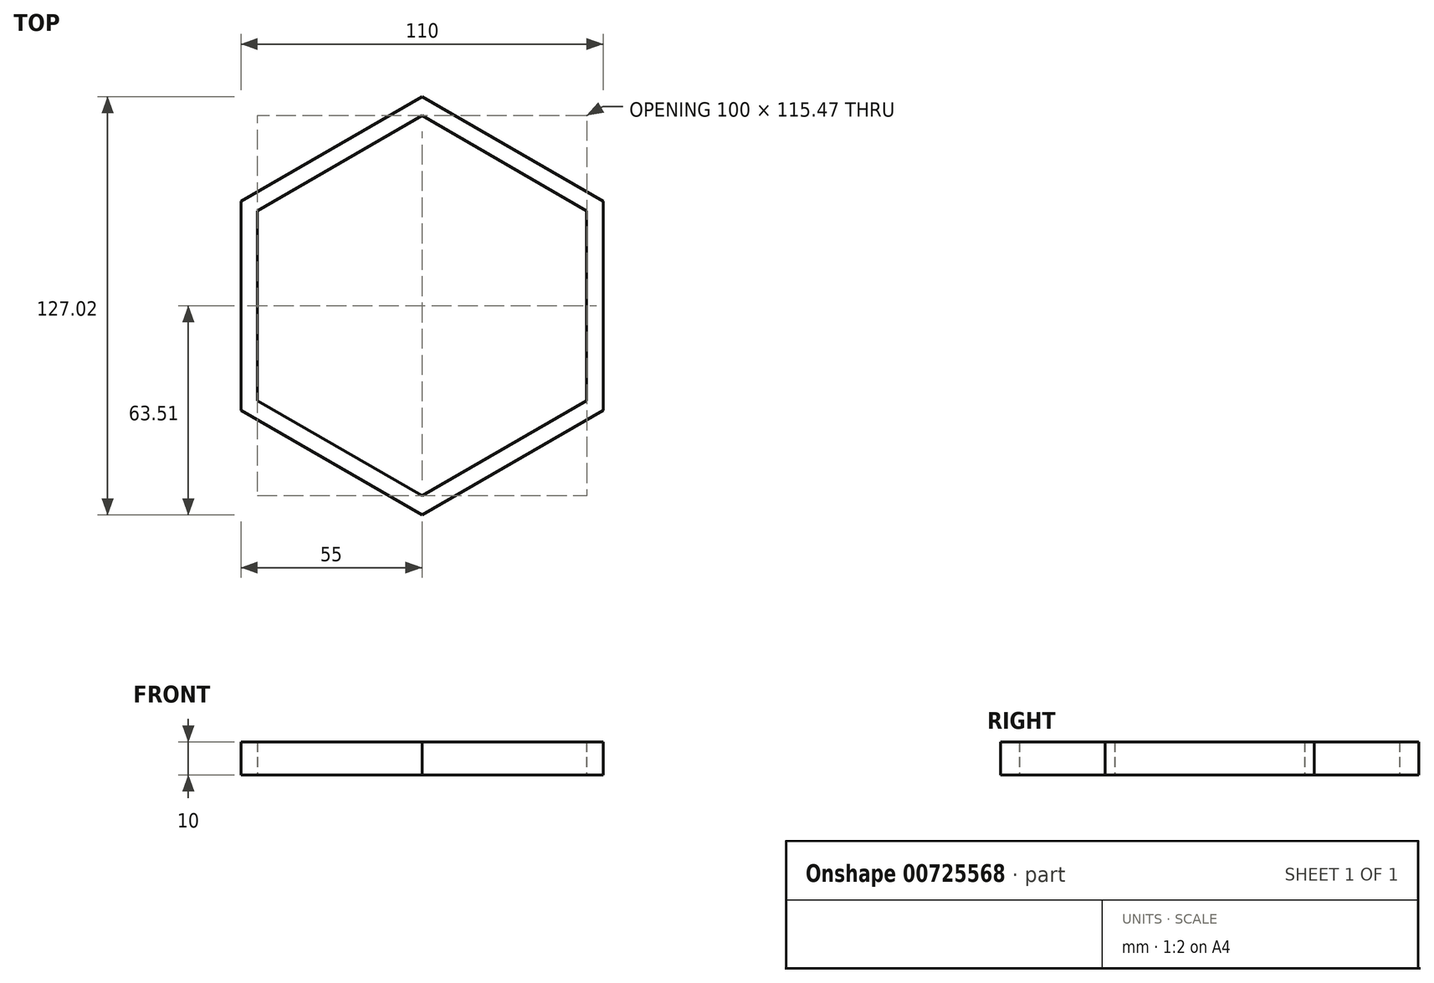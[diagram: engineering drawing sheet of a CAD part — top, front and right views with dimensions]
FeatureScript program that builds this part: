
annotation { "Feature Type Name" : "Feature", "Feature Type Description" : "" }
export const myFeature = defineFeature(function(context is Context, id is Id, definition is map)
    precondition{}
    {
        {
            var Q0;
            Q0=qCreatedBy(makeId("Top.planeOp"),FACE);
            var sketch = newSketch(context, id + "F0", { "sketchPlane" : qUnion([Q0])});
            skCircle(sketch, "E0.cCircle", {"center": v(0, 0) * mm, "radius": 50 * mm, "construction": true});
            skLineSegment(sketch, "E0.0", {"start": v(50, 28.87) * mm, "end": v(50, -28.87) * mm});
            skLineSegment(sketch, "E0.1", {"start": v(50, -28.87) * mm, "end": v(0, -57.74) * mm});
            skLineSegment(sketch, "E0.2", {"start": v(0, -57.74) * mm, "end": v(-50, -28.87) * mm});
            skLineSegment(sketch, "E0.3", {"start": v(-50, -28.87) * mm, "end": v(-50, 28.87) * mm});
            skLineSegment(sketch, "E0.4", {"start": v(-50, 28.87) * mm, "end": v(0, 57.74) * mm});
            skLineSegment(sketch, "E0.5", {"start": v(0, 57.74) * mm, "end": v(50, 28.87) * mm});
            skPoint(sketch, "E0.0.midPoint", {"position": v(50, 0) * mm});
            skCircle(sketch, "E1.cCircle", {"center": v(0, 0) * mm, "radius": 55 * mm, "construction": true});
            skLineSegment(sketch, "E1.0", {"start": v(55, 31.75) * mm, "end": v(55, -31.75) * mm});
            skLineSegment(sketch, "E1.1", {"start": v(55, -31.75) * mm, "end": v(0, -63.5) * mm});
            skLineSegment(sketch, "E1.2", {"start": v(0, -63.5) * mm, "end": v(-55, -31.75) * mm});
            skLineSegment(sketch, "E1.3", {"start": v(-55, -31.75) * mm, "end": v(-55, 31.75) * mm});
            skLineSegment(sketch, "E1.4", {"start": v(-55, 31.75) * mm, "end": v(0, 63.5) * mm});
            skLineSegment(sketch, "E1.5", {"start": v(0, 63.5) * mm, "end": v(55, 31.75) * mm});
            skPoint(sketch, "E1.0.midPoint", {"position": v(55, 0) * mm});
            skSolve(sketch);
        }
        {
            var Q0;
            Q0=makeQuery(id+"F0.imprint","IMPRINT",FACE,{"disambiguationData":[TD([[makeQuery(id+"F0.imprint","IMPRINT",EDGE,{"derivedFrom":sQuery(id+"F0.wireOp",EDGE,"E0.0")}),1.0]])]});
            extrude(context, id + "F1", {"entities" : qUnion([Q0]), "depth" : 10 * mm, "offsetDistance" : 25.4 * mm});
        }
    });
